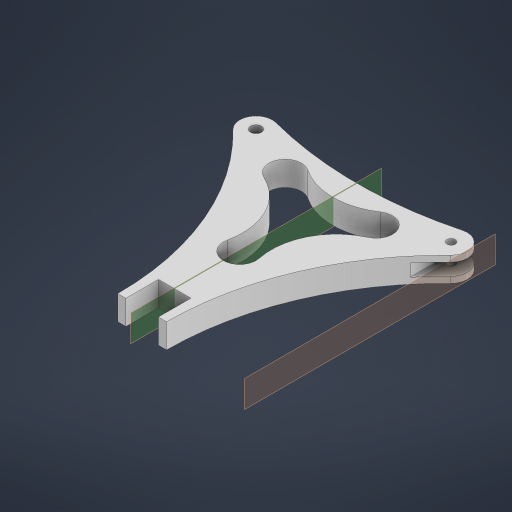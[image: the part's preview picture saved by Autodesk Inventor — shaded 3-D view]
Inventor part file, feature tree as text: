
AUTODESK INVENTOR PART (.ipt)
format: ipt  version: 2024 (Build 280153000, 153)  size: 316,416 bytes
history: native  units: mm
features: other x8, extrude x2, sketch x2, mirror x1
ambient origin geometry x8: Origin, YZ Plane, XZ Plane, XY Plane, X Axis, Y Axis, Z Axis, Center Point
bodies: Body1 (feature_tree)
feature tree (13):
  other  "Твердое тело1"
  extrude  "Выдавливание1"  Depth=20.0mm
  other  "РабПлоскость2"
  extrude  "Выдавливание3"  Depth=120.0mm
  other  "Непосредственное редактирование1"
  other  "РабПлоскость3"
  mirror  "Зеркальное отражение1"
  other  "Непосредственное редактирование2"
  sketch  "Эскиз1"
  sketch  "Эскиз3"
  other  "РабПлоскость4"
  other  "Перенос1"
  other  "Перенос2"
